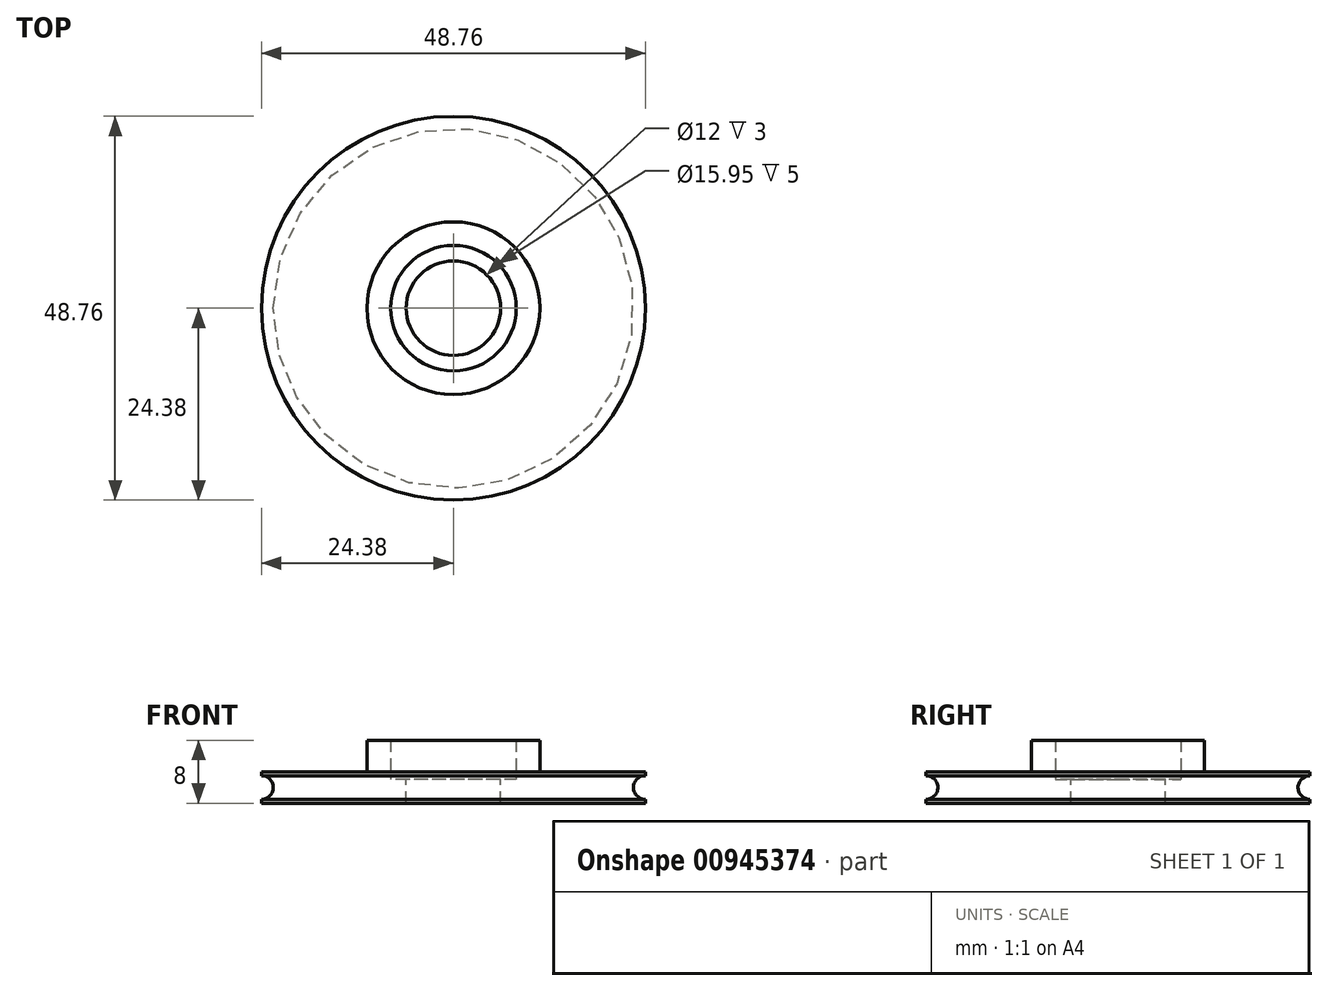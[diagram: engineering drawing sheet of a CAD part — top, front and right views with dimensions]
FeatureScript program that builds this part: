
annotation { "Feature Type Name" : "Feature", "Feature Type Description" : "" }
export const myFeature = defineFeature(function(context is Context, id is Id, definition is map)
    precondition{}
    {
        {
            var Q0;
            Q0=qCreatedBy(makeId("Top.planeOp"),FACE);
            var sketch = newSketch(context, id + "F0", { "sketchPlane" : qUnion([Q0])});
            skCircle(sketch, "E0", {"center": v(0, 0) * mm, "radius": 24.38 * mm});
            skSolve(sketch);
        }
        {
            var Q0;
            Q0=makeQuery(id+"F0.imprint","IMPRINT",FACE,{"disambiguationData":[TD([[makeQuery(id+"F0.imprint","IMPRINT",EDGE,{"derivedFrom":sQuery(id+"F0.wireOp",EDGE,"E0")}),1.0]])]});
            extrude(context, id + "F1", {"entities" : qUnion([Q0]), "depth" : 4 * mm, "offsetDistance" : 25.4 * mm});
        }
        {
            var Q0;
            Q0=makeQuery(id+"F1.opExtrude","CAP_FACE",FACE,{"disambiguationData":[OSD([sQuery(id+"F0.wireOp",EDGE,"E0"),sQuery(id+"F0.wireOp",EDGE,"n39IqKt5-bk1q-LU1x-fgod-8OyBNiFTd7FZ")])],"isStart":false});
            var sketch = newSketch(context, id + "F2", { "sketchPlane" : qUnion([Q0])});
            skCircle(sketch, "E1", {"center": v(0, 0) * mm, "radius": 7.97 * mm});
            skCircle(sketch, "E2.0", {"center": v(0, 0) * mm, "radius": 10.97 * mm});
            skSolve(sketch);
        }
        {
            var Q0;
            Q0=qSketchRegion(id+"F2",true);
            extrude(context, id + "F3", {"entities" : qUnion([Q0]), "operationType" : NewBodyOperationType.ADD, "depth" : 4 * mm, "offsetDistance" : 25.4 * mm});
        }
        {
            var Q0;
            Q0=makeQuery(id+"F3.boolean.opBoolean","SPLIT",FACE,{"disambiguationData":[TD([makeQuery(id+"F3.opExtrude","SWEPT_FACE",FACE,{"disambiguationData":[OSD([sQuery(id+"F2.wireOp",EDGE,"E1")])]})])],"derivedFrom":makeQuery(id+"F1.opExtrude","CAP_FACE",FACE,{"disambiguationData":[OSD([sQuery(id+"F0.wireOp",EDGE,"E0")])],"isStart":false})});
            var sketch = newSketch(context, id + "F4", { "sketchPlane" : qUnion([Q0])});
            skCircle(sketch, "E3", {"center": v(0, 0) * mm, "radius": 6 * mm});
            skSolve(sketch);
        }
        {
            var Q0;
            Q0=makeQuery(id+"F4.imprint","IMPRINT",FACE,{"disambiguationData":[TD([[makeQuery(id+"F4.imprint","IMPRINT",EDGE,{"derivedFrom":sQuery(id+"F4.wireOp",EDGE,"E3")}),1.0]])]});
            var Q1;
            Q1=makeQuery(id+"F4.imprint","IMPRINT",FACE,{"disambiguationData":[TD([[makeQuery(id+"F4.imprint","IMPRINT",EDGE,{"derivedFrom":makeQuery(id+"FgYK8jIepfClWtA_1.opExtrude","CAP_EDGE",EDGE,{"disambiguationData":[OSD([sQuery(id+"F8DXjnVyigKkjng_1.wireOp",EDGE,"EUjAMsCd-Zx2B-3j4q-cP5o-T3GrjTijNDqK")])],"isStart":false})}),1.0]])]});
            extrude(context, id + "F5", {"entities" : qUnion([Q0, Q1]), "operationType" : NewBodyOperationType.REMOVE, "oppositeDirection" : true, "depth" : 9 * mm, "offsetDistance" : 25.4 * mm});
        }
        {
            var Q0;
            Q0=qCreatedBy(makeId("Front.planeOp"),FACE);
            var sketch = newSketch(context, id + "F6", { "sketchPlane" : qUnion([Q0])});
            skCircle(sketch, "E4", {"center": v(-24.38, 2) * mm, "radius": 1.5 * mm});
            skLineSegment(sketch, "E5.bottom", {"start": v(-22.88, 0.65) * mm, "end": v(-25.02, 0.65) * mm});
            skLineSegment(sketch, "E5.top", {"start": v(-22.88, 3.35) * mm, "end": v(-25.02, 3.35) * mm});
            skLineSegment(sketch, "E5.left", {"start": v(-22.88, 0.65) * mm, "end": v(-22.88, 3.35) * mm});
            skLineSegment(sketch, "E5.right", {"start": v(-25.73, 1.35) * mm, "end": v(-25.73, 2.65) * mm});
            skLineSegment(sketch, "E6", {"start": v(0, 19.1) * mm, "end": v(0, -12.61) * mm, "construction": true});
            skLineSegment(sketch, "E7", {"start": v(-24.37, 3.35) * mm, "end": v(-22.88, 2) * mm});
            skLineSegment(sketch, "E8", {"start": v(-22.88, 2) * mm, "end": v(-24.38, 0.65) * mm});
            skLineSegment(sketch, "E9", {"start": v(-24.38, 0.65) * mm, "end": v(-24.37, 3.35) * mm});
            skSolve(sketch);
        }
        {
            var Q0;
            {var subQ0=sQuery(id+"F6.wireOp",EDGE,"E5.top");var subQ1=sQuery(id+"F6.wireOp",EDGE,"E4");var subQ2=makeQuery(id+"F6.imprint","INTERSECT",VERTEX,{"disambiguationData":[OD(0.0)],"derivedFrom":[subQ1,subQ0]});Q0=makeQuery(id+"F6.imprint","IMPRINT",FACE,{"disambiguationData":[TD([[makeQuery(id+"F6.imprint","IMPRINT",EDGE,{"disambiguationData":[TD([[subQ2,1.0]])],"derivedFrom":subQ1}),1.0]])]});}
            var Q1;
            {var subQ0=sQuery(id+"F6.wireOp",EDGE,"E5.bottom");var subQ1=sQuery(id+"F6.wireOp",EDGE,"E4");var subQ2=makeQuery(id+"F6.imprint","INTERSECT",VERTEX,{"disambiguationData":[OD(0.0)],"derivedFrom":[subQ1,subQ0]});Q1=makeQuery(id+"F6.imprint","IMPRINT",FACE,{"disambiguationData":[TD([[makeQuery(id+"F6.imprint","IMPRINT",EDGE,{"disambiguationData":[TD([[subQ2,-1.0]])],"derivedFrom":subQ1}),1.0]])]});}
            var Q2;
            {var subQ4=sQuery(id+"F6.wireOp",EDGE,"E5.right");Q2=makeQuery(id+"F6.imprint","IMPRINT",FACE,{"disambiguationData":[TD([[makeQuery(id+"F6.imprint","IMPRINT",EDGE,{"derivedFrom":subQ4}),-1.0]])]});}
            var Q3;
            {var subQ0=sQuery(id+"F6.wireOp",EDGE,"E7");Q3=makeQuery(id+"F6.imprint","IMPRINT",FACE,{"disambiguationData":[TD([[makeQuery(id+"F6.imprint","IMPRINT",EDGE,{"derivedFrom":subQ0}),1.0]])]});}
            var Q4;
            Q4=makeQuery(id+"F6.imprint","IMPRINT",FACE,{"disambiguationData":[TD([[makeQuery(id+"F6.imprint","IMPRINT",EDGE,{"derivedFrom":sQuery(id+"F6.wireOp",EDGE,"E7")}),-1.0]])]});
            var Q5;
            {var subQ0=sQuery(id+"F6.wireOp",EDGE,"E8");Q5=makeQuery(id+"F6.imprint","IMPRINT",FACE,{"disambiguationData":[TD([[makeQuery(id+"F6.imprint","IMPRINT",EDGE,{"derivedFrom":subQ0}),1.0]])]});}
            var Q6;
            Q6=sQuery(id+"F6.wireOp",EDGE,"E6");
            revolve(context, id + "F7", {"operationType" : NewBodyOperationType.REMOVE, "surfaceOperationType" : NewSurfaceOperationType.NEW, "entities" : qUnion([Q0, Q1, Q2, Q3, Q4, Q5]), "axis" : qUnion([Q6]), "revolveType" : RevolveType.FULL, "oppositeDirection" : true});
        }
        {
            var Q0;
            Q0=makeQuery(id+"F3.boolean.opBoolean","SPLIT",FACE,{"disambiguationData":[TD([makeQuery(id+"F3.opExtrude","SWEPT_FACE",FACE,{"disambiguationData":[OSD([sQuery(id+"F2.wireOp",EDGE,"E1")])]})])],"derivedFrom":makeQuery(id+"F1.opExtrude","CAP_FACE",FACE,{"disambiguationData":[OSD([sQuery(id+"F0.wireOp",EDGE,"E0")])],"isStart":false})});
            extrude(context, id + "F8", {"entities" : qUnion([Q0]), "operationType" : NewBodyOperationType.REMOVE, "oppositeDirection" : true, "depth" : 1 * mm, "offsetDistance" : 25 * mm});
        }
    });
